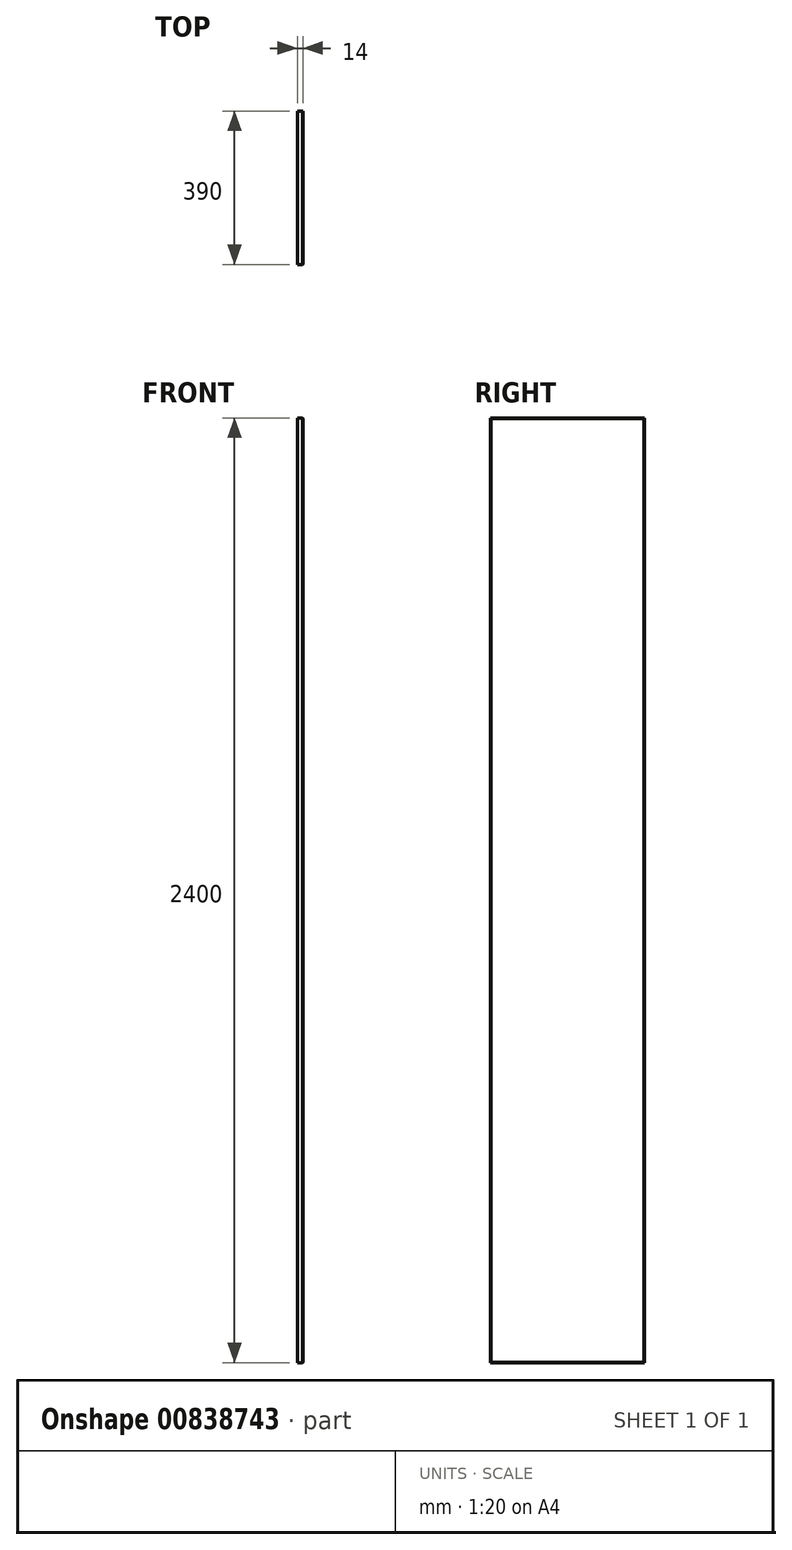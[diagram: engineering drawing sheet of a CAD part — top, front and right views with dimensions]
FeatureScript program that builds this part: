
annotation { "Feature Type Name" : "Feature", "Feature Type Description" : "" }
export const myFeature = defineFeature(function(context is Context, id is Id, definition is map)
    precondition{}
    {
        {
            var Q0;
            Q0=qCreatedBy(makeId("Right.planeOp"),FACE);
            var sketch = newSketch(context, id + "F0", { "sketchPlane" : qUnion([Q0])});
            skLineSegment(sketch, "E0.bottom", {"start": v(0, 0) * mm, "end": v(-55.42, 0) * mm});
            skLineSegment(sketch, "E0.top", {"start": v(0, 42.97) * mm, "end": v(-55.42, 42.97) * mm});
            skLineSegment(sketch, "E0.left", {"start": v(0, 0) * mm, "end": v(0, 42.97) * mm});
            skLineSegment(sketch, "E0.right", {"start": v(-55.42, 0) * mm, "end": v(-55.42, 42.97) * mm});
            skSolve(sketch);
        }
        {
            var Q0;
            Q0=makeQuery(id+"F0.imprint","IMPRINT",FACE,{"disambiguationData":[TD([[makeQuery(id+"F0.imprint","IMPRINT",EDGE,{"derivedFrom":sQuery(id+"F0.wireOp",EDGE,"E0.bottom")}),-1.0]])]});
            extrude(context, id + "F1", {"entities" : qUnion([Q0]), "oppositeDirection" : true, "depth" : 14 * mm, "offsetDistance" : 25 * mm});
        }
        {
            var Q0;
            Q0=makeQuery(id+"F1.opExtrude","SWEPT_FACE",FACE,{"disambiguationData":[OSD([sQuery(id+"F0.wireOp",EDGE,"E0.bottom")])]});
            extrude(context, id + "F2", {"entities" : qUnion([Q0]), "operationType" : NewBodyOperationType.ADD, "oppositeDirection" : true, "depth" : 1060 * mm, "offsetDistance" : 25 * mm});
        }
        {
            var Q0;
            {var subQ0=sQuery(id+"F0.wireOp",EDGE,"E0.left");Q0=makeQuery(id+"F2.boolean.opBoolean","MERGE",FACE,{"derivedFrom":[makeQuery(id+"F1.opExtrude","SWEPT_FACE",FACE,{"disambiguationData":[OSD([subQ0])]}),makeQuery(id+"F2.opExtrude","SWEPT_FACE",FACE,{"disambiguationData":[OSD([sQuery(id+"F0.wireOp",EDGE,"E0.bottom"),subQ0])]})]});}
            extrude(context, id + "F3", {"entities" : qUnion([Q0]), "operationType" : NewBodyOperationType.ADD, "oppositeDirection" : true, "depth" : 390 * mm, "offsetDistance" : 25 * mm});
        }
        {
            var Q0;
            {var subQ0=sQuery(id+"F0.wireOp",EDGE,"E0.left");var subQ1=sQuery(id+"F0.wireOp",EDGE,"E0.bottom");Q0=makeQuery(id+"F3.boolean.opBoolean","MERGE",FACE,{"derivedFrom":[makeQuery(id+"F2.opExtrude","CAP_FACE",FACE,{"disambiguationData":[OSD([subQ1])],"isStart":false}),makeQuery(id+"F3.opExtrude","SWEPT_FACE",FACE,{"disambiguationData":[OSD([subQ1,subQ0]),TDD([makeQuery(id+"F2.opExtrude","CAP_EDGE",EDGE,{"disambiguationData":[OSD([subQ1,subQ0])],"isStart":false})])]})]});}
            extrude(context, id + "F4", {"entities" : qUnion([Q0]), "operationType" : NewBodyOperationType.ADD, "depth" : 1340 * mm, "offsetDistance" : 25 * mm});
        }
        {
            var Q0;
            {var subQ0=sQuery(id+"F0.wireOp",EDGE,"E0.left");var subQ1=sQuery(id+"F0.wireOp",EDGE,"E0.bottom");var subQ2=makeQuery(id+"F1.opExtrude","CAP_VERTEX",VERTEX,{"disambiguationData":[OSD([subQ1,subQ0])],"isStart":true});var subQ3=makeQuery(id+"F1.opExtrude","CAP_EDGE",EDGE,{"disambiguationData":[OSD([subQ1])],"isStart":true});Q0=makeQuery(id+"F4.boolean.opBoolean","MERGE",FACE,{"derivedFrom":[makeQuery(id+"F3.boolean.opBoolean","MERGE",FACE,{"derivedFrom":[makeQuery(id+"F2.boolean.opBoolean","MERGE",FACE,{"derivedFrom":[makeQuery(id+"F1.opExtrude","CAP_FACE",FACE,{"disambiguationData":[OSD([subQ1,sQuery(id+"F0.wireOp",EDGE,"E0.top"),subQ0,sQuery(id+"F0.wireOp",EDGE,"E0.right")])],"isStart":true}),makeQuery(id+"F2.opExtrude","SWEPT_FACE",FACE,{"disambiguationData":[OSD([subQ1]),TDD([subQ3])]})]}),makeQuery(id+"F3.opExtrude","SWEPT_FACE",FACE,{"disambiguationData":[OSD([subQ1,subQ0]),TDD([makeQuery(id+"F2.boolean.opBoolean","MERGE",EDGE,{"derivedFrom":[makeQuery(id+"F1.opExtrude","CAP_EDGE",EDGE,{"disambiguationData":[OSD([subQ0])],"isStart":true}),makeQuery(id+"F2.opExtrude","SWEPT_EDGE",EDGE,{"disambiguationData":[OSD([subQ1,subQ0]),TDD([subQ2])]})]})])]})]}),makeQuery(id+"F4.opExtrude","SWEPT_FACE",FACE,{"disambiguationData":[OSD([subQ1,subQ0]),TDD([makeQuery(id+"F3.boolean.opBoolean","MERGE",EDGE,{"derivedFrom":[makeQuery(id+"F2.opExtrude","CAP_EDGE",EDGE,{"disambiguationData":[OSD([subQ1]),TDD([subQ3])],"isStart":false}),makeQuery(id+"F3.opExtrude","SWEPT_EDGE",EDGE,{"disambiguationData":[OSD([subQ1,subQ0]),TDD([makeQuery(id+"F2.opExtrude","CAP_VERTEX",VERTEX,{"disambiguationData":[OSD([subQ1,subQ0]),TDD([subQ2])],"isStart":false})])]})]})])]})]});}
            var Q1;
            {var subQ0=sQuery(id+"F0.wireOp",EDGE,"E0.left");var subQ1=sQuery(id+"F0.wireOp",EDGE,"E0.bottom");var subQ2=makeQuery(id+"F1.opExtrude","CAP_VERTEX",VERTEX,{"disambiguationData":[OSD([subQ1,subQ0])],"isStart":false});var subQ3=makeQuery(id+"F1.opExtrude","CAP_EDGE",EDGE,{"disambiguationData":[OSD([subQ1])],"isStart":false});Q1=makeQuery(id+"F4.boolean.opBoolean","MERGE",FACE,{"derivedFrom":[makeQuery(id+"F3.boolean.opBoolean","MERGE",FACE,{"derivedFrom":[makeQuery(id+"F2.boolean.opBoolean","MERGE",FACE,{"derivedFrom":[makeQuery(id+"F1.opExtrude","CAP_FACE",FACE,{"disambiguationData":[OSD([subQ1,sQuery(id+"F0.wireOp",EDGE,"E0.top"),subQ0,sQuery(id+"F0.wireOp",EDGE,"E0.right")])],"isStart":false}),makeQuery(id+"F2.opExtrude","SWEPT_FACE",FACE,{"disambiguationData":[OSD([subQ1]),TDD([subQ3])]})]}),makeQuery(id+"F3.opExtrude","SWEPT_FACE",FACE,{"disambiguationData":[OSD([subQ1,subQ0]),TDD([makeQuery(id+"F2.boolean.opBoolean","MERGE",EDGE,{"derivedFrom":[makeQuery(id+"F1.opExtrude","CAP_EDGE",EDGE,{"disambiguationData":[OSD([subQ0])],"isStart":false}),makeQuery(id+"F2.opExtrude","SWEPT_EDGE",EDGE,{"disambiguationData":[OSD([subQ1,subQ0]),TDD([subQ2])]})]})])]})]}),makeQuery(id+"F4.opExtrude","SWEPT_FACE",FACE,{"disambiguationData":[OSD([subQ1,subQ0]),TDD([makeQuery(id+"F3.boolean.opBoolean","MERGE",EDGE,{"derivedFrom":[makeQuery(id+"F2.opExtrude","CAP_EDGE",EDGE,{"disambiguationData":[OSD([subQ1]),TDD([subQ3])],"isStart":false}),makeQuery(id+"F3.opExtrude","SWEPT_EDGE",EDGE,{"disambiguationData":[OSD([subQ1,subQ0]),TDD([makeQuery(id+"F2.opExtrude","CAP_VERTEX",VERTEX,{"disambiguationData":[OSD([subQ1,subQ0]),TDD([subQ2])],"isStart":false})])]})]})])]})]});}
            chamfer(context, id + "F5", {"entities" : qUnion([Q0, Q1]), "width" : 1 * mm, "tangentPropagation" : true});
        }
    });
